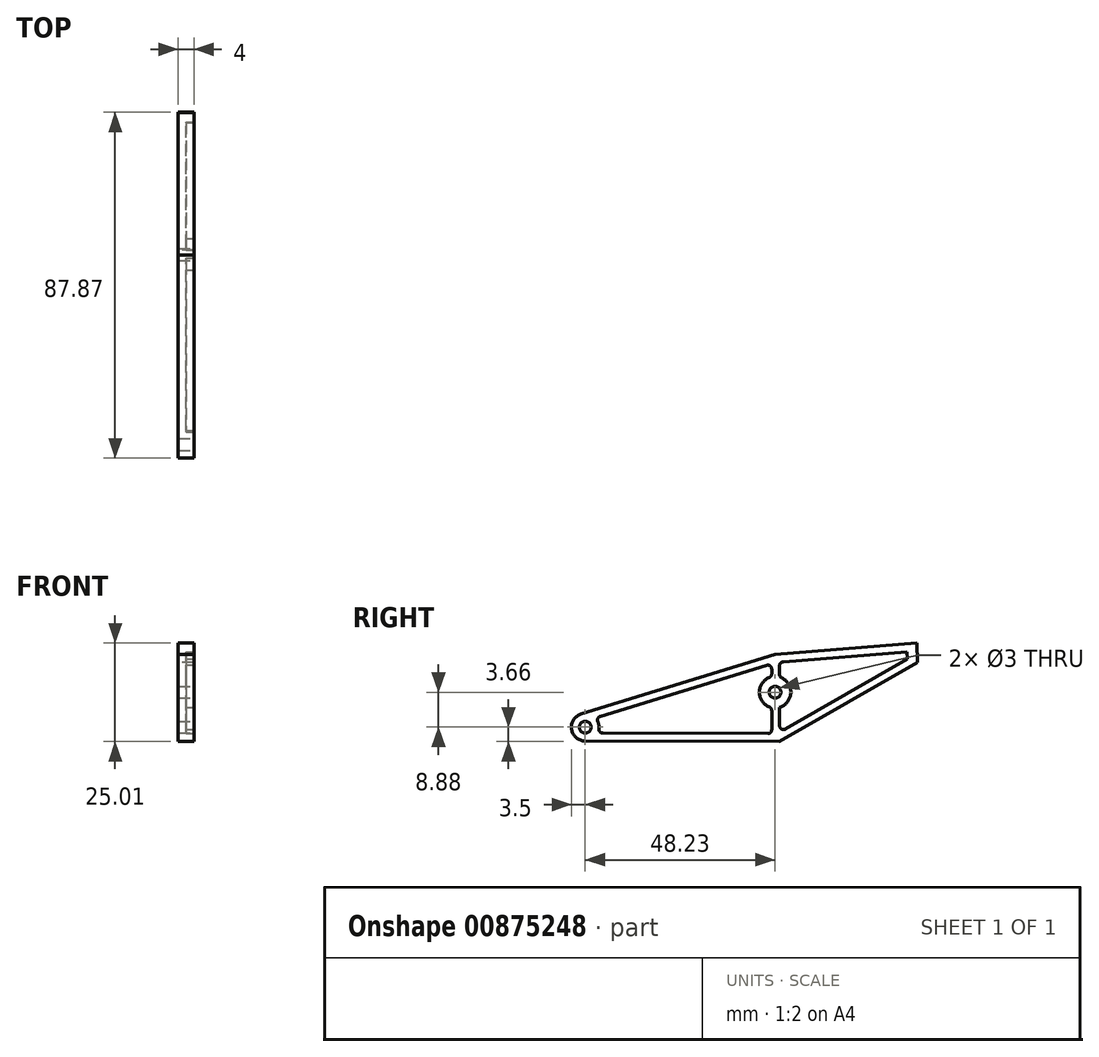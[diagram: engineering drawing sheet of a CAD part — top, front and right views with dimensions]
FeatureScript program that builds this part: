
annotation { "Feature Type Name" : "Feature", "Feature Type Description" : "" }
export const myFeature = defineFeature(function(context is Context, id is Id, definition is map)
    precondition{}
    {
        {
            var Q0;
            Q0=qCreatedBy(makeId("Right.planeOp"),FACE);
            var sketch = newSketch(context, id + "F0", { "sketchPlane" : qUnion([Q0])});
            skArc(sketch, "E0", {"start": v(-1.03, 3.35) * mm, "mid": v(-3.46, -0.51) * mm, "end": v(-0.01, -3.5) * mm});
            skLineSegment(sketch, "E1", {"start": v(-1.03, 3.35) * mm, "end": v(48.14, 18.44) * mm});
            skLineSegment(sketch, "E2", {"start": v(48.14, 18.44) * mm, "end": v(84.24, 21.35) * mm});
            skLineSegment(sketch, "E3", {"start": v(84.24, 21.35) * mm, "end": v(84.37, 16.43) * mm});
            skLineSegment(sketch, "E4", {"start": v(84.37, 16.43) * mm, "end": v(49.38, -3.66) * mm});
            skLineSegment(sketch, "E5", {"start": v(49.38, -3.66) * mm, "end": v(-0.01, -3.5) * mm});
            skSolve(sketch);
        }
        {
            var Q0;
            Q0 = qSketchRegion(id + "F0", true);
            extrude(context, id + "F1", {"entities" : qUnion([Q0]), "depth" : 4 * mm, "offsetDistance" : 25 * mm});
        }
        {
            var Q0;
            Q0=makeQuery(id+"F1.opExtrude","CAP_FACE",FACE,{"disambiguationData":[OSD([sQuery(id+"F0.wireOp",EDGE,"E0"),sQuery(id+"F0.wireOp",EDGE,"E1"),sQuery(id+"F0.wireOp",EDGE,"E2"),sQuery(id+"F0.wireOp",EDGE,"E3"),sQuery(id+"F0.wireOp",EDGE,"E4"),sQuery(id+"F0.wireOp",EDGE,"E5")])],"isStart":false});
            var sketch = newSketch(context, id + "F2", { "sketchPlane" : qUnion([Q0])});
            skArc(sketch, "E6", {"start": v(46.75, 12.6) * mm, "mid": v(44.23, 8.88) * mm, "end": v(46.75, 5.16) * mm});
            skLineSegment(sketch, "E7", {"start": v(47.38, 13.53) * mm, "end": v(47.38, 14.76) * mm});
            skLineSegment(sketch, "E8", {"start": v(46.09, 15.72) * mm, "end": v(3.83, 2.75) * mm});
            skArc(sketch, "E9", {"start": v(3.48, -0.4) * mm, "mid": v(3.46, 0.51) * mm, "end": v(3.21, 1.4) * mm});
            skLineSegment(sketch, "E10", {"start": v(4.47, -1.51) * mm, "end": v(46.38, -1.65) * mm});
            skLineSegment(sketch, "E11", {"start": v(47.38, 4.23) * mm, "end": v(47.38, -0.65) * mm});
            skLineSegment(sketch, "E12", {"start": v(49.38, 13.4) * mm, "end": v(49.38, 15.61) * mm});
            skLineSegment(sketch, "E13", {"start": v(50.3, 16.6) * mm, "end": v(81.8, 19.15) * mm});
            skLineSegment(sketch, "E14", {"start": v(81.8, 19.15) * mm, "end": v(81.85, 17.29) * mm});
            skLineSegment(sketch, "E15", {"start": v(81.85, 17.29) * mm, "end": v(50.88, -0.5) * mm});
            skLineSegment(sketch, "E16", {"start": v(49.38, 0.37) * mm, "end": v(49.38, 5.05) * mm});
            skArc(sketch, "E17.trimOffspring", {"start": v(49.38, 5.05) * mm, "mid": v(52.22, 8.57) * mm, "end": v(49.95, 12.5) * mm});
            skPoint(sketch, "E18.visualSharp", {"position": v(2.58, 2.36) * mm});
            skArc(sketch, "E18.filletArc", {"start": v(3.83, 2.75) * mm, "mid": v(3.22, 2.2) * mm, "end": v(3.21, 1.4) * mm});
            skPoint(sketch, "E19.visualSharp", {"position": v(3.16, -1.51) * mm});
            skArc(sketch, "E19.filletArc", {"start": v(3.48, -0.4) * mm, "mid": v(3.72, -1.18) * mm, "end": v(4.47, -1.51) * mm});
            skPoint(sketch, "E20.visualSharp", {"position": v(47.38, 16.11) * mm});
            skArc(sketch, "E20.filletArc", {"start": v(47.38, 14.76) * mm, "mid": v(46.97, 15.57) * mm, "end": v(46.09, 15.72) * mm});
            skPoint(sketch, "E21.visualSharp", {"position": v(47.38, 12.79) * mm});
            skArc(sketch, "E21.filletArc", {"start": v(46.75, 12.6) * mm, "mid": v(47.2, 12.96) * mm, "end": v(47.38, 13.53) * mm});
            skPoint(sketch, "E22.visualSharp", {"position": v(47.38, 4.97) * mm});
            skArc(sketch, "E22.filletArc", {"start": v(47.38, 4.23) * mm, "mid": v(47.2, 4.8) * mm, "end": v(46.75, 5.16) * mm});
            skPoint(sketch, "E23.visualSharp", {"position": v(49.38, 12.71) * mm});
            skArc(sketch, "E23.filletArc", {"start": v(49.38, 13.4) * mm, "mid": v(49.53, 12.86) * mm, "end": v(49.95, 12.5) * mm});
            skPoint(sketch, "E24.visualSharp", {"position": v(49.38, 16.53) * mm});
            skArc(sketch, "E24.filletArc", {"start": v(50.3, 16.6) * mm, "mid": v(49.65, 16.29) * mm, "end": v(49.38, 15.61) * mm});
            skPoint(sketch, "E25.visualSharp", {"position": v(49.38, -1.35) * mm});
            skArc(sketch, "E25.filletArc", {"start": v(49.38, 0.37) * mm, "mid": v(49.88, -0.5) * mm, "end": v(50.88, -0.5) * mm});
            skPoint(sketch, "E26.visualSharp", {"position": v(47.38, -1.65) * mm});
            skArc(sketch, "E26.filletArc", {"start": v(46.38, -1.65) * mm, "mid": v(47.09, -1.36) * mm, "end": v(47.38, -0.65) * mm});
            skSolve(sketch);
        }
        {
            var Q0;
            Q0 = qSketchRegion(id + "F2", true);
            extrude(context, id + "F3", {"entities" : qUnion([Q0]), "operationType" : NewBodyOperationType.REMOVE, "oppositeDirection" : true, "depth" : 2 * mm, "offsetDistance" : 25 * mm});
        }
        {
            var Q0;
            Q0=makeQuery(id+"F1.opExtrude","CAP_FACE",FACE,{"disambiguationData":[OSD([sQuery(id+"F0.wireOp",EDGE,"E0"),sQuery(id+"F0.wireOp",EDGE,"E1"),sQuery(id+"F0.wireOp",EDGE,"E2"),sQuery(id+"F0.wireOp",EDGE,"E3"),sQuery(id+"F0.wireOp",EDGE,"E4"),sQuery(id+"F0.wireOp",EDGE,"E5")])],"isStart":false});
            var sketch = newSketch(context, id + "F4", { "sketchPlane" : qUnion([Q0])});
            skCircle(sketch, "E27", {"center": v(0, 0) * mm, "radius": 1.5 * mm});
            skCircle(sketch, "E28", {"center": v(48.23, 8.88) * mm, "radius": 1.5 * mm});
            skSolve(sketch);
        }
        {
            var Q0;
            Q0 = qSketchRegion(id + "F4", true);
            extrude(context, id + "F5", {"entities" : qUnion([Q0]), "operationType" : NewBodyOperationType.REMOVE, "endBound" : BoundingType.THROUGH_ALL, "oppositeDirection" : true, "depth" : 25 * mm, "offsetDistance" : 25 * mm});
        }
    });
